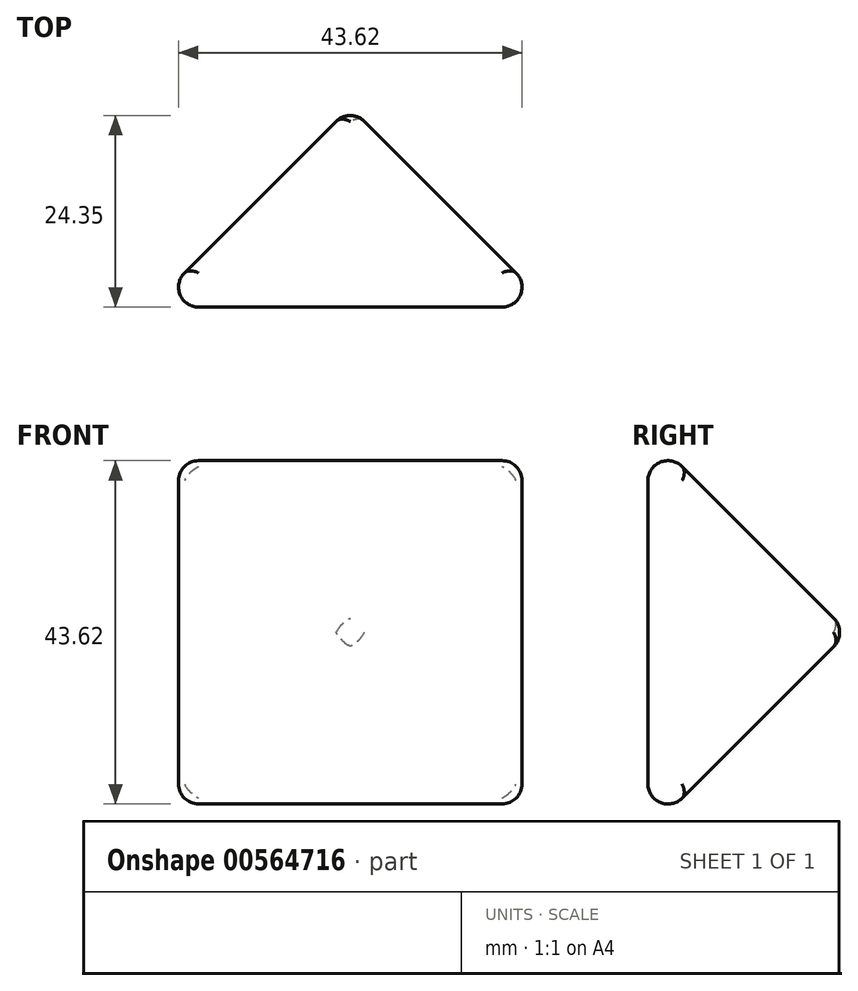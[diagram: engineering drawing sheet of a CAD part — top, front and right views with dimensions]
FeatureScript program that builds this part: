
annotation { "Feature Type Name" : "Feature", "Feature Type Description" : "" }
export const myFeature = defineFeature(function(context is Context, id is Id, definition is map)
    precondition{}
    {
        {
            var Q0;
            Q0=qCreatedBy(makeId("Front.planeOp"),FACE);
            cPlane(context, id + "F0", {"entities" : qUnion([Q0]), "cplaneType" : CPlaneType.OFFSET, "offset" : 25.4 * mm, "width" : 152.4 * mm, "height" : 152.4 * mm});
        }
        {
            var Q0;
            Q0=qCreatedBy(id+"F0.planeOp",FACE);
            var sketch = newSketch(context, id + "F1", { "sketchPlane" : qUnion([Q0])});
            skLineSegment(sketch, "E0.bottom", {"start": v(25.4, -25.4) * mm, "end": v(-25.4, -25.4) * mm});
            skLineSegment(sketch, "E0.top", {"start": v(25.4, 25.4) * mm, "end": v(-25.4, 25.4) * mm});
            skLineSegment(sketch, "E0.left", {"start": v(25.4, -25.4) * mm, "end": v(25.4, 25.4) * mm});
            skLineSegment(sketch, "E0.right", {"start": v(-25.4, -25.4) * mm, "end": v(-25.4, 25.4) * mm});
            skPoint(sketch, "E0.middle", {"position": v(0, 0) * mm});
            skSolve(sketch);
        }
        {
            var Q0;
            Q0=makeQuery(id+"F1.imprint","IMPRINT",FACE,{"disambiguationData":[TD([[makeQuery(id+"F1.imprint","IMPRINT",EDGE,{"derivedFrom":sQuery(id+"F1.wireOp",EDGE,"E0.bottom")}),-1.0]])]});
            var Q1;
            Q1=qCreatedBy(makeId("Origin.pointOp"),VERTEX);
            loft(context, id + "F2", {"sheetProfilesArray" : [{ "sheetProfileEntities" : qUnion([Q0]) }, { "sheetProfileEntities" : qUnion([Q1]) }]});
        }
        {
            var Q0;
            Q0=makeQuery(id+"F2.opLoft","CAP_FACE",FACE,{"disambiguationData":[OSD([makeQuery(id+"F1.imprint","IMPRINT",FACE,{"disambiguationData":[TD([[makeQuery(id+"F1.imprint","IMPRINT",EDGE,{"derivedFrom":sQuery(id+"F1.wireOp",EDGE,"E0.bottom")}),-1.0]])]})])],"isStart":true});
            var Q1;
            Q1=makeQuery(id+"F2.opLoft","SWEPT_FACE",FACE,{"disambiguationData":[OSD([sQuery(id+"F1.wireOp",EDGE,"E0.bottom"),sQuery(id+"F1.wireOp",EDGE,"E0.left"),sQuery(id+"F1.wireOp",EDGE,"E0.right")])]});
            var Q2;
            Q2=makeQuery(id+"F2.opLoft","SWEPT_FACE",FACE,{"disambiguationData":[OSD([sQuery(id+"F1.wireOp",EDGE,"E0.top"),sQuery(id+"F1.wireOp",EDGE,"E0.left"),sQuery(id+"F1.wireOp",EDGE,"E0.right")])]});
            fillet(context, id + "F3", {"entities" : qUnion([Q0, Q1, Q2]), "radius" : 2.54 * mm, "tangentPropagation" : true, "allowEdgeOverflow" : false});
        }
    });
